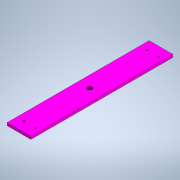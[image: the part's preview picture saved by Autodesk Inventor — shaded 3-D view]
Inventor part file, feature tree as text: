
AUTODESK INVENTOR PART (.ipt)
format: ipt  version: 2022 (Build 260153000, 153)  size: 115,200 bytes
history: native  units: mm
features: extrude x1, sketch x1
ambient origin geometry x8: Origin, YZ Plane, XZ Plane, XY Plane, X Axis, Y Axis, Z Axis, Center Point
bodies: Body1 (feature_tree)
feature tree (2):
  extrude  "Extrusion2"  Depth=6.0mm
  sketch  "Sketch1"  dims[d0=10.0mm d3=4.0mm d4=4.0mm d6=50.0mm d7=300.0mm d9=9.4mm d11=260.0mm d12=20.0mm d15=3.0mm d16=10.0mm d17=3.0mm d18=6.0mm d19=0.0mm]
